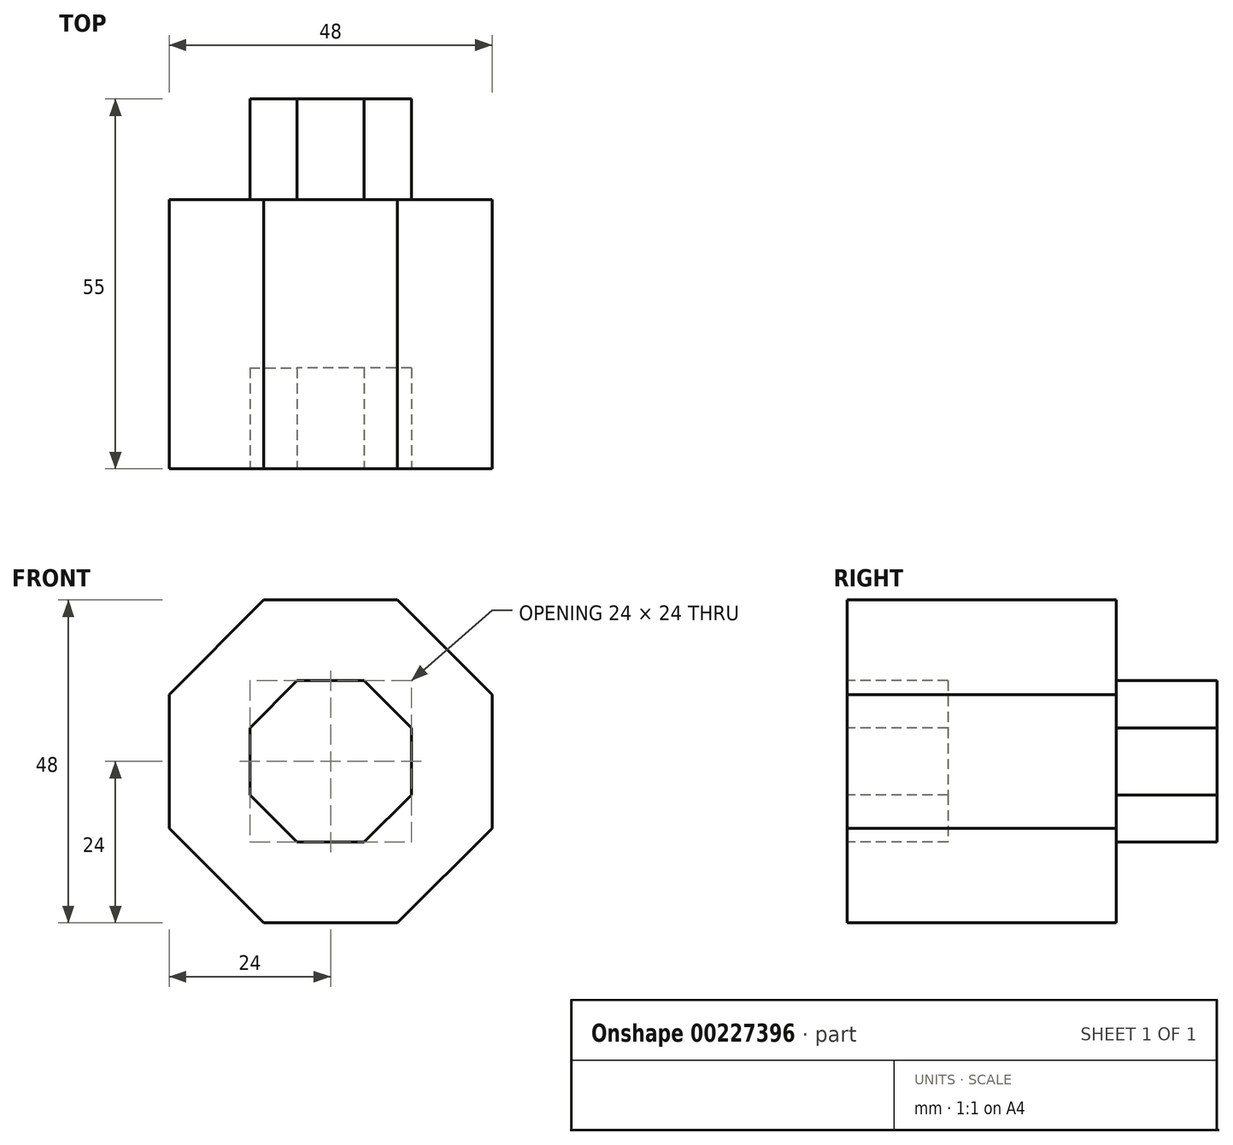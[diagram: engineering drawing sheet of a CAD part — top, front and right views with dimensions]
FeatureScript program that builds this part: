
annotation { "Feature Type Name" : "Feature", "Feature Type Description" : "" }
export const myFeature = defineFeature(function(context is Context, id is Id, definition is map)
    precondition{}
    {
        {
            var Q0;
            Q0=qCreatedBy(makeId("Front.planeOp"),FACE);
            var sketch = newSketch(context, id + "F0", { "sketchPlane" : qUnion([Q0])});
            skLineSegment(sketch, "E0.0", {"start": v(24, 9.94) * mm, "end": v(24, -9.94) * mm});
            skLineSegment(sketch, "E0.1", {"start": v(24, -9.94) * mm, "end": v(9.94, -24) * mm});
            skLineSegment(sketch, "E0.2", {"start": v(9.94, -24) * mm, "end": v(-9.94, -24) * mm});
            skLineSegment(sketch, "E0.3", {"start": v(-9.94, -24) * mm, "end": v(-24, -9.94) * mm});
            skLineSegment(sketch, "E0.4", {"start": v(-24, -9.94) * mm, "end": v(-24, 9.94) * mm});
            skLineSegment(sketch, "E0.5", {"start": v(-24, 9.94) * mm, "end": v(-9.94, 24) * mm});
            skLineSegment(sketch, "E0.6", {"start": v(-9.94, 24) * mm, "end": v(9.94, 24) * mm});
            skLineSegment(sketch, "E0.7", {"start": v(9.94, 24) * mm, "end": v(24, 9.94) * mm});
            skSolve(sketch);
        }
        {
            var Q0;
            Q0 = qSketchRegion(id + "F0", true);
            extrude(context, id + "F1", {"entities" : qUnion([Q0]), "depth" : 40 * mm});
        }
        {
            var Q0;
            Q0=qCreatedBy(makeId("Front.planeOp"),FACE);
            var sketch = newSketch(context, id + "F2", { "sketchPlane" : qUnion([Q0])});
            skLineSegment(sketch, "E1.0", {"start": v(12, -4.97) * mm, "end": v(4.97, -12) * mm});
            skLineSegment(sketch, "E1.1", {"start": v(4.97, -12) * mm, "end": v(-4.97, -12) * mm});
            skLineSegment(sketch, "E1.2", {"start": v(-4.97, -12) * mm, "end": v(-12, -4.97) * mm});
            skLineSegment(sketch, "E1.3", {"start": v(-12, -4.97) * mm, "end": v(-12, 4.97) * mm});
            skLineSegment(sketch, "E1.4", {"start": v(-12, 4.97) * mm, "end": v(-4.97, 12) * mm});
            skLineSegment(sketch, "E1.5", {"start": v(-4.97, 12) * mm, "end": v(4.97, 12) * mm});
            skLineSegment(sketch, "E1.6", {"start": v(4.97, 12) * mm, "end": v(12, 4.97) * mm});
            skLineSegment(sketch, "E1.7", {"start": v(12, 4.97) * mm, "end": v(12, -4.97) * mm});
            skSolve(sketch);
        }
        {
            var Q0;
            Q0=makeQuery(id+"F2.imprint","IMPRINT",FACE,{"disambiguationData":[TD([[makeQuery(id+"F2.imprint","IMPRINT",EDGE,{"derivedFrom":sQuery(id+"F2.wireOp",EDGE,"E1.0")}),-1.0]])]});
            extrude(context, id + "F3", {"entities" : qUnion([Q0]), "operationType" : NewBodyOperationType.ADD, "oppositeDirection" : true, "depth" : 15 * mm});
        }
        {
            var Q0;
            Q0=makeQuery(id+"F1.opExtrude","CAP_FACE",FACE,{"disambiguationData":[OSD([sQuery(id+"F0.wireOp",EDGE,"E0.0"),sQuery(id+"F0.wireOp",EDGE,"E0.1"),sQuery(id+"F0.wireOp",EDGE,"E0.2"),sQuery(id+"F0.wireOp",EDGE,"E0.3"),sQuery(id+"F0.wireOp",EDGE,"E0.4"),sQuery(id+"F0.wireOp",EDGE,"E0.5"),sQuery(id+"F0.wireOp",EDGE,"E0.6"),sQuery(id+"F0.wireOp",EDGE,"E0.7")])],"isStart":false});
            var sketch = newSketch(context, id + "F4", { "sketchPlane" : qUnion([Q0])});
            skLineSegment(sketch, "E2.0", {"start": v(4.97, -12) * mm, "end": v(-4.97, -12) * mm});
            skLineSegment(sketch, "E2.1", {"start": v(-4.97, -12) * mm, "end": v(-12, -4.97) * mm});
            skLineSegment(sketch, "E2.2", {"start": v(-12, -4.97) * mm, "end": v(-12, 4.97) * mm});
            skLineSegment(sketch, "E2.3", {"start": v(-12, 4.97) * mm, "end": v(-4.97, 12) * mm});
            skLineSegment(sketch, "E2.4", {"start": v(-4.97, 12) * mm, "end": v(4.97, 12) * mm});
            skLineSegment(sketch, "E2.5", {"start": v(4.97, 12) * mm, "end": v(12, 4.97) * mm});
            skLineSegment(sketch, "E2.6", {"start": v(12, 4.97) * mm, "end": v(12, -4.97) * mm});
            skLineSegment(sketch, "E2.7", {"start": v(12, -4.97) * mm, "end": v(4.97, -12) * mm});
            skSolve(sketch);
        }
        {
            var Q0;
            Q0=makeQuery(id+"F4.imprint","IMPRINT",FACE,{"disambiguationData":[TD([[makeQuery(id+"F4.imprint","IMPRINT",EDGE,{"derivedFrom":sQuery(id+"F4.wireOp",EDGE,"E2.0")}),-1.0]])]});
            extrude(context, id + "F5", {"entities" : qUnion([Q0]), "operationType" : NewBodyOperationType.REMOVE, "oppositeDirection" : true, "depth" : 15 * mm});
        }
    });
